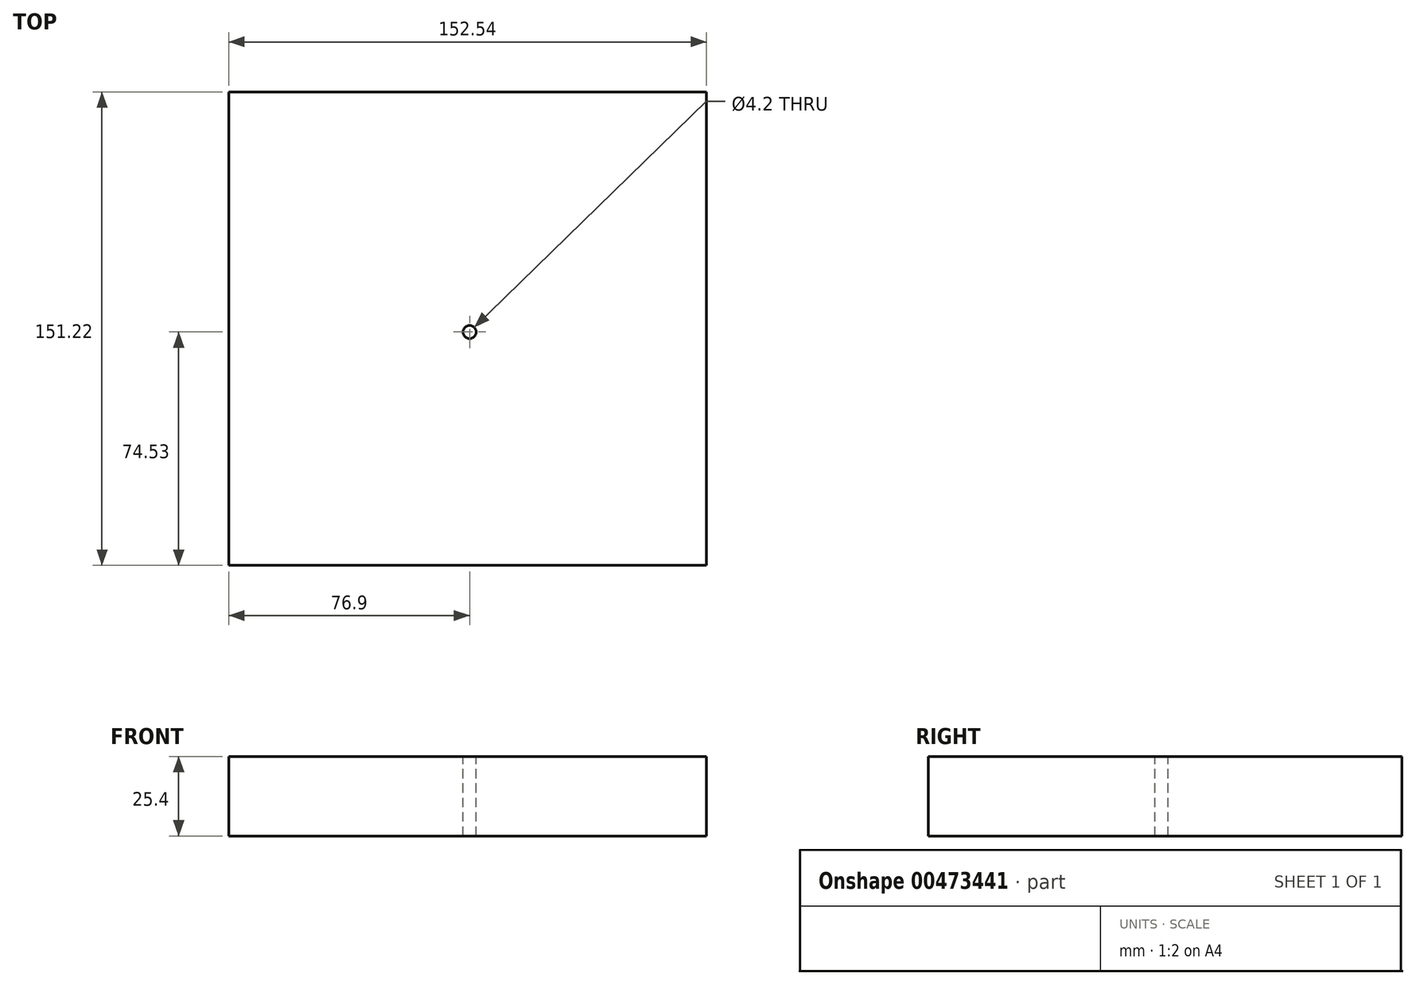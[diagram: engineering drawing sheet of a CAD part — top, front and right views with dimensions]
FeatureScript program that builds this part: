
annotation { "Feature Type Name" : "Feature", "Feature Type Description" : "" }
export const myFeature = defineFeature(function(context is Context, id is Id, definition is map)
    precondition{}
    {
        {
            var Q0;
            Q0=qCreatedBy(makeId("Top.planeOp"),FACE);
            var sketch = newSketch(context, id + "F0", { "sketchPlane" : qUnion([Q0])});
            skLineSegment(sketch, "E0", {"start": v(75.64, 0) * mm, "end": v(75.64, 76.7) * mm});
            skLineSegment(sketch, "E1", {"start": v(75.64, 76.7) * mm, "end": v(-76.9, 76.7) * mm});
            skLineSegment(sketch, "E2", {"start": v(-76.9, 76.7) * mm, "end": v(-76.9, -74.53) * mm});
            skLineSegment(sketch, "E3", {"start": v(-76.9, -74.53) * mm, "end": v(75.64, -74.53) * mm});
            skLineSegment(sketch, "E4", {"start": v(75.64, -74.53) * mm, "end": v(75.64, 0) * mm});
            skSolve(sketch);
        }
        {
            var Q0;
            Q0=makeQuery(id+"F0.imprint","IMPRINT",FACE,{"disambiguationData":[TD([[makeQuery(id+"F0.imprint","IMPRINT",EDGE,{"derivedFrom":sQuery(id+"F0.wireOp",EDGE,"E0")}),1.0]])]});
            extrude(context, id + "F1", {"entities" : qUnion([Q0]), "oppositeDirection" : true, "depth" : 25.4 * mm});
        }
        {
            var Q0;
            Q0=makeQuery(id+"F1.opExtrude","CAP_FACE",FACE,{"disambiguationData":[OSD([sQuery(id+"F0.wireOp",EDGE,"E0"),sQuery(id+"F0.wireOp",EDGE,"E1"),sQuery(id+"F0.wireOp",EDGE,"E2"),sQuery(id+"F0.wireOp",EDGE,"E3"),sQuery(id+"F0.wireOp",EDGE,"E4")])],"isStart":true});
            var sketch = newSketch(context, id + "F2", { "sketchPlane" : qUnion([Q0])});
            skPoint(sketch, "E5", {"position": v(0, 0) * mm});
            skSolve(sketch);
        }
        {
            var Q0;
            Q0=sQuery(id+"F2.wireOp",VERTEX,"E5");
            var Q1;
            Q1=makeQuery(id+"F1.opExtrude","SWEPT_BODY",BODY,{"disambiguationData":[OSD([sQuery(id+"F0.wireOp",EDGE,"E0"),sQuery(id+"F0.wireOp",EDGE,"E1"),sQuery(id+"F0.wireOp",EDGE,"E2"),sQuery(id+"F0.wireOp",EDGE,"E3"),sQuery(id+"F0.wireOp",EDGE,"E4")])]});
            hole(context, id + "F3", {"style" : HoleStyle.SIMPLE, "endStyle" : HoleEndStyle.THROUGH, "standardTappedOrClearance" : lookupTablePath({ "standard" : "ISO", "engagement" : "75%", "pitch" : "0.8 mm", "size" : "M5", "type" : "Tapped" }), "standardBlindInLast" : lookupTablePath({ "standard" : "ISO", "engagement" : "75%", "pitch" : "0.8 mm", "size" : "M5", "type" : "Tapped" }), "holeDiameter" : 4.2 * mm, "showTappedDepth" : true, "tappedDepth" : 12.7 * mm, "tapClearance" : 3, "locations" : qUnion([Q0]), "scope" : qUnion([Q1]), "majorDiameter" : 5 * mm});
        }
    });
